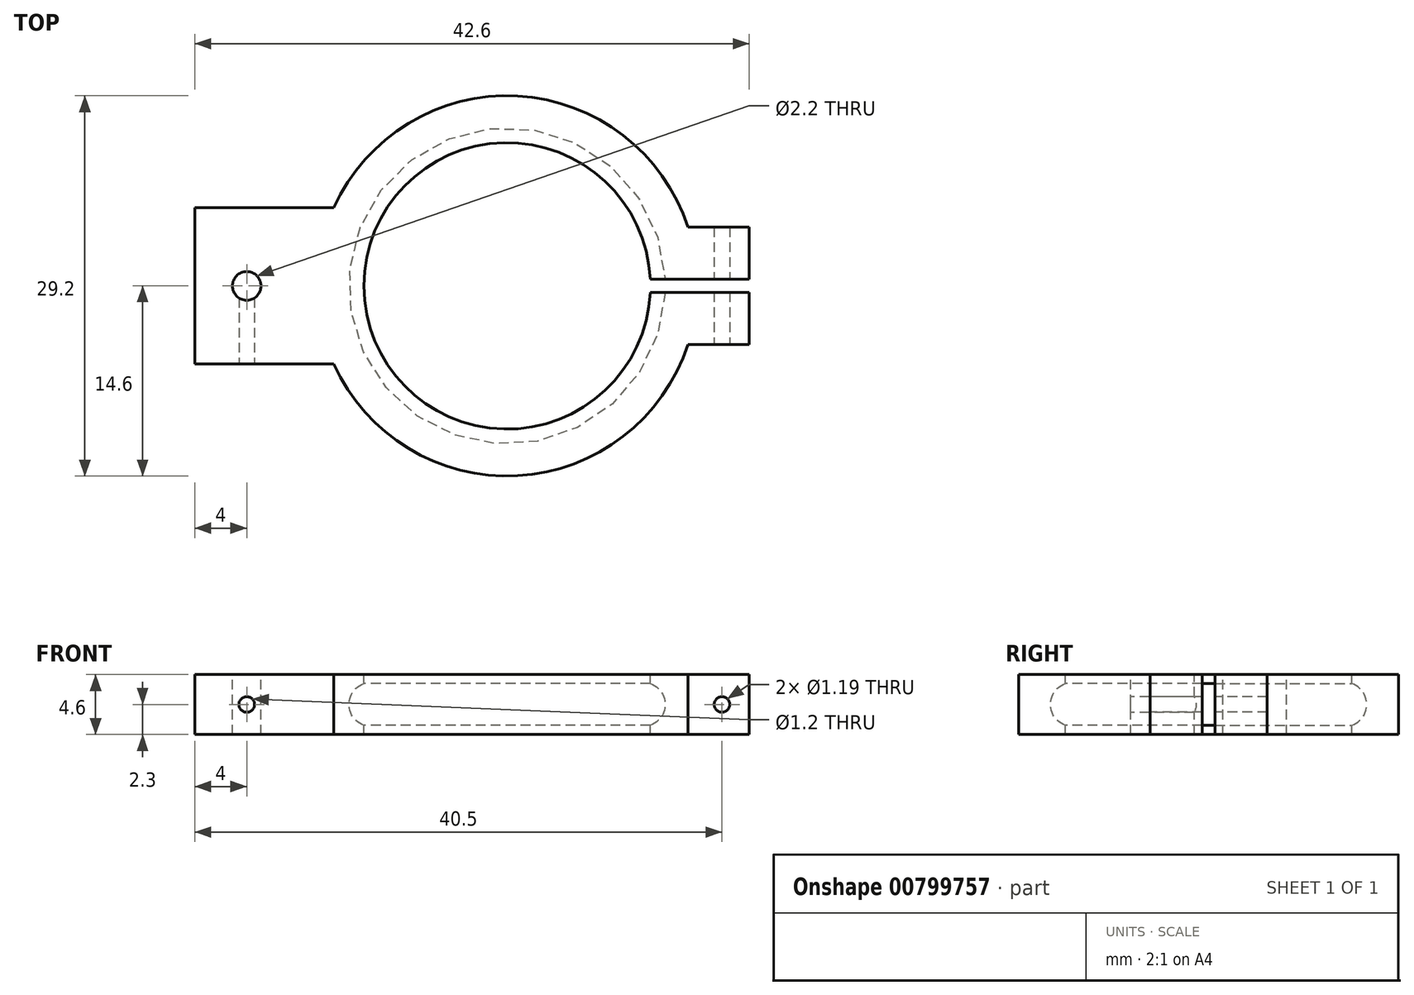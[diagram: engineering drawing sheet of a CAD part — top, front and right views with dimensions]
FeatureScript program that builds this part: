
annotation { "Feature Type Name" : "Feature", "Feature Type Description" : "" }
export const myFeature = defineFeature(function(context is Context, id is Id, definition is map)
    precondition{}
    {
        {
            var Q0;
            Q0=qCreatedBy(makeId("Front.planeOp"),FACE);
            var sketch = newSketch(context, id + "F0", { "sketchPlane" : qUnion([Q0])});
            skCircle(sketch, "E0", {"center": v(-17.36, 10.12) * mm, "radius": 2.3 * mm});
            skLineSegment(sketch, "E1", {"start": v(-6.36, 16.76) * mm, "end": v(-6.36, -1.05) * mm});
            skLineSegment(sketch, "E2", {"start": v(-17.36, 12.42) * mm, "end": v(-17.36, 7.82) * mm});
            skLineSegment(sketch, "E3", {"start": v(-17.36, 11.72) * mm, "end": v(-19.01, 11.72) * mm});
            skLineSegment(sketch, "E4", {"start": v(-17.36, 8.52) * mm, "end": v(-19.01, 8.52) * mm});
            skLineSegment(sketch, "E5", {"start": v(-18.5, 10.78) * mm, "end": v(-18.5, 9.2) * mm});
            skArc(sketch, "E6", {"start": v(-17.36, 11.72) * mm, "mid": v(-18.5, 10.12) * mm, "end": v(-17.36, 8.52) * mm});
            skLineSegment(sketch, "E7", {"start": v(-17.36, 12.42) * mm, "end": v(-20.96, 12.42) * mm});
            skLineSegment(sketch, "E8", {"start": v(-20.96, 12.42) * mm, "end": v(-20.96, 7.82) * mm});
            skLineSegment(sketch, "E9", {"start": v(-20.96, 7.82) * mm, "end": v(-17.36, 7.82) * mm});
            skSolve(sketch);
        }
        {
            var Q0;
            {var subQ3=sQuery(id+"F0.wireOp",EDGE,"E3");Q0=makeQuery(id+"F0.imprint","IMPRINT",FACE,{"disambiguationData":[TD([[makeQuery(id+"F0.imprint","IMPRINT",EDGE,{"derivedFrom":subQ3}),-1.0]])]});}
            var Q1;
            {var subQ0=sQuery(id+"F0.wireOp",EDGE,"E3");Q1=makeQuery(id+"F0.imprint","IMPRINT",FACE,{"disambiguationData":[TD([[makeQuery(id+"F0.imprint","IMPRINT",EDGE,{"derivedFrom":subQ0}),1.0]])]});}
            var Q2;
            {var subQ3=sQuery(id+"F0.wireOp",EDGE,"E4");Q2=makeQuery(id+"F0.imprint","IMPRINT",FACE,{"disambiguationData":[TD([[makeQuery(id+"F0.imprint","IMPRINT",EDGE,{"derivedFrom":subQ3}),1.0]])]});}
            var Q3;
            {var subQ5=sQuery(id+"F0.wireOp",EDGE,"E7");Q3=makeQuery(id+"F0.imprint","IMPRINT",FACE,{"disambiguationData":[TD([[makeQuery(id+"F0.imprint","IMPRINT",EDGE,{"derivedFrom":subQ5}),1.0]])]});}
            var Q4;
            Q4=sQuery(id+"F0.wireOp",EDGE,"E1");
            revolve(context, id + "F1", {"surfaceOperationType" : NewSurfaceOperationType.NEW, "entities" : qUnion([Q0, Q1, Q2, Q3]), "axis" : qUnion([Q4]), "revolveType" : RevolveType.FULL});
        }
        {
            var Q0;
            Q0=makeQuery(id+"F1.opRevolve","SWEPT_FACE",FACE,{"disambiguationData":[OSD([sQuery(id+"F0.wireOp",EDGE,"E7")])]});
            var sketch = newSketch(context, id + "F2", { "sketchPlane" : qUnion([Q0])});
            skLineSegment(sketch, "E10.bottom", {"start": v(-18.78, 6) * mm, "end": v(-30.36, 6) * mm});
            skLineSegment(sketch, "E10.top", {"start": v(-18.78, -6) * mm, "end": v(-30.36, -6) * mm});
            skLineSegment(sketch, "E10.left", {"start": v(-18.78, 6) * mm, "end": v(-18.78, -6) * mm});
            skLineSegment(sketch, "E10.right", {"start": v(-30.36, 6) * mm, "end": v(-30.36, -6) * mm});
            skLineSegment(sketch, "E11.bottom", {"start": v(6.47, 4.5) * mm, "end": v(12.24, 4.5) * mm});
            skLineSegment(sketch, "E11.top", {"start": v(6.47, -4.5) * mm, "end": v(12.24, -4.5) * mm});
            skLineSegment(sketch, "E11.left", {"start": v(6.47, 4.5) * mm, "end": v(6.47, -4.5) * mm});
            skLineSegment(sketch, "E11.right", {"start": v(12.24, 4.5) * mm, "end": v(12.24, -4.5) * mm});
            skLineSegment(sketch, "E12", {"start": v(6.47, 0.5) * mm, "end": v(12.24, 0.5) * mm});
            skLineSegment(sketch, "E13", {"start": v(6.47, -0.5) * mm, "end": v(12.24, -0.5) * mm});
            skPoint(sketch, "E14", {"position": v(-6.36, 0) * mm});
            skCircle(sketch, "E15", {"center": v(-26.36, 0) * mm, "radius": 1.1 * mm});
            skSolve(sketch);
        }
        {
            var Q0;
            {var subQ0=sQuery(id+"F2.wireOp",EDGE,"E10.left");Q0=makeQuery(id+"F2.imprint","IMPRINT",FACE,{"disambiguationData":[TD([[makeQuery(id+"F2.imprint","IMPRINT",EDGE,{"derivedFrom":subQ0}),-1.0]])]});}
            var Q1;
            {var subQ0=sQuery(id+"F2.wireOp",EDGE,"E11.right");var subQ1=sQuery(id+"F2.wireOp",EDGE,"E11.bottom");var subQ2=makeQuery(id+"F2.imprint","INTERSECT",VERTEX,{"derivedFrom":[subQ1,subQ0]});Q1=makeQuery(id+"F2.imprint","IMPRINT",FACE,{"disambiguationData":[TD([[makeQuery(id+"F2.imprint","IMPRINT",EDGE,{"disambiguationData":[TD([[subQ2,-1.0]])],"derivedFrom":subQ0}),-1.0]])]});}
            var Q2;
            {var subQ0=sQuery(id+"F2.wireOp",EDGE,"E11.right");var subQ1=sQuery(id+"F2.wireOp",EDGE,"E11.top");var subQ2=makeQuery(id+"F2.imprint","INTERSECT",VERTEX,{"derivedFrom":[subQ1,subQ0]});Q2=makeQuery(id+"F2.imprint","IMPRINT",FACE,{"disambiguationData":[TD([[makeQuery(id+"F2.imprint","IMPRINT",EDGE,{"disambiguationData":[TD([[subQ2,1.0]])],"derivedFrom":subQ0}),-1.0]])]});}
            var Q3;
            {var subQ0=sQuery(id+"F2.wireOp",EDGE,"E11.left");var subQ1=sQuery(id+"F2.wireOp",EDGE,"E11.bottom");var subQ2=makeQuery(id+"F2.imprint","INTERSECT",VERTEX,{"derivedFrom":[subQ1,subQ0]});Q3=makeQuery(id+"F2.imprint","IMPRINT",FACE,{"disambiguationData":[TD([[makeQuery(id+"F2.imprint","IMPRINT",EDGE,{"disambiguationData":[TD([[subQ2,-1.0]])],"derivedFrom":subQ0}),1.0]])]});}
            var Q4;
            {var subQ0=sQuery(id+"F2.wireOp",EDGE,"E11.left");var subQ1=sQuery(id+"F2.wireOp",EDGE,"E11.top");var subQ2=makeQuery(id+"F2.imprint","INTERSECT",VERTEX,{"derivedFrom":[subQ1,subQ0]});Q4=makeQuery(id+"F2.imprint","IMPRINT",FACE,{"disambiguationData":[TD([[makeQuery(id+"F2.imprint","IMPRINT",EDGE,{"disambiguationData":[TD([[subQ2,1.0]])],"derivedFrom":subQ0}),1.0]])]});}
            var Q5;
            {var subQ0=sQuery(id+"F2.wireOp",EDGE,"E12");var subQ1=sQuery(id+"F2.wireOp",EDGE,"E11.right");var subQ2=makeQuery(id+"F2.imprint","INTERSECT",VERTEX,{"derivedFrom":[subQ1,subQ0]});Q5=makeQuery(id+"F2.imprint","IMPRINT",FACE,{"disambiguationData":[TD([[makeQuery(id+"F2.imprint","IMPRINT",EDGE,{"disambiguationData":[TD([[subQ2,-1.0]])],"derivedFrom":subQ1}),-1.0]])]});}
            var Q6;
            {var subQ0=sQuery(id+"F2.wireOp",EDGE,"E12");var subQ1=sQuery(id+"F2.wireOp",EDGE,"E11.left");var subQ2=makeQuery(id+"F2.imprint","INTERSECT",VERTEX,{"derivedFrom":[subQ1,subQ0]});Q6=makeQuery(id+"F2.imprint","IMPRINT",FACE,{"disambiguationData":[TD([[makeQuery(id+"F2.imprint","IMPRINT",EDGE,{"disambiguationData":[TD([[subQ2,-1.0]])],"derivedFrom":subQ1}),1.0]])]});}
            var Q7;
            {var subQ0=sQuery(id+"F2.wireOp",EDGE,"E10.right");Q7=makeQuery(id+"F2.imprint","IMPRINT",FACE,{"disambiguationData":[TD([[makeQuery(id+"F2.imprint","IMPRINT",EDGE,{"derivedFrom":subQ0}),1.0]])]});}
            extrude(context, id + "F3", {"entities" : qUnion([Q0, Q1, Q2, Q3, Q4, Q5, Q6, Q7]), "operationType" : NewBodyOperationType.ADD, "oppositeDirection" : true, "depth" : 4.6 * mm, "offsetDistance" : 25 * mm});
        }
        {
            var Q0;
            Q0=makeQuery(id+"F3.opExtrude","SWEPT_FACE",FACE,{"disambiguationData":[OSD([sQuery(id+"F2.wireOp",EDGE,"E10.top")])]});
            var sketch = newSketch(context, id + "F4", { "sketchPlane" : qUnion([Q0])});
            skCircle(sketch, "E16", {"center": v(-26.36, 10.12) * mm, "radius": 0.6 * mm});
            skPoint(sketch, "E16.centerSnap0", {"position": v(-30.36, 10.12) * mm});
            skSolve(sketch);
        }
        {
            var Q0;
            Q0=makeQuery(id+"F4.imprint","IMPRINT",FACE,{"disambiguationData":[TD([[makeQuery(id+"F4.imprint","IMPRINT",EDGE,{"derivedFrom":sQuery(id+"F4.wireOp",EDGE,"E16")}),1.0]])]});
            extrude(context, id + "F5", {"entities" : qUnion([Q0]), "operationType" : NewBodyOperationType.REMOVE, "oppositeDirection" : true, "depth" : 6 * mm, "offsetDistance" : 25 * mm});
        }
        {
            var Q0;
            Q0=makeQuery(id+"F3.opExtrude","SWEPT_FACE",FACE,{"disambiguationData":[OSD([sQuery(id+"F2.wireOp",EDGE,"E11.top")])]});
            var sketch = newSketch(context, id + "F6", { "sketchPlane" : qUnion([Q0])});
            skCircle(sketch, "E17", {"center": v(10.14, 10.12) * mm, "radius": 0.6 * mm});
            skPoint(sketch, "E17.centerSnap0", {"position": v(12.24, 10.12) * mm});
            skSolve(sketch);
        }
        {
            var Q0;
            Q0=makeQuery(id+"F6.imprint","IMPRINT",FACE,{"disambiguationData":[TD([[makeQuery(id+"F6.imprint","IMPRINT",EDGE,{"derivedFrom":sQuery(id+"F6.wireOp",EDGE,"E17")}),1.0]])]});
            extrude(context, id + "F7", {"entities" : qUnion([Q0]), "operationType" : NewBodyOperationType.REMOVE, "oppositeDirection" : true, "depth" : 25 * mm, "offsetDistance" : 25 * mm});
        }
        {
            var Q0;
            Q0=makeQuery(id+"F3.boolean.opBoolean","MERGE",FACE,{"derivedFrom":[makeQuery(id+"F1.opRevolve","SWEPT_FACE",FACE,{"disambiguationData":[OSD([sQuery(id+"F0.wireOp",EDGE,"E7")])]}),makeQuery(id+"F3.opExtrude","CAP_FACE",FACE,{"disambiguationData":[OSD([sQuery(id+"F2.wireOp",EDGE,"E10.bottom"),sQuery(id+"F2.wireOp",EDGE,"E10.top"),sQuery(id+"F2.wireOp",EDGE,"E10.left"),sQuery(id+"F2.wireOp",EDGE,"E10.right"),sQuery(id+"F2.wireOp",EDGE,"E15")])],"isStart":true}),makeQuery(id+"F3.opExtrude","CAP_FACE",FACE,{"disambiguationData":[OSD([sQuery(id+"F2.wireOp",EDGE,"E11.bottom"),sQuery(id+"F2.wireOp",EDGE,"E11.top"),sQuery(id+"F2.wireOp",EDGE,"E11.left"),sQuery(id+"F2.wireOp",EDGE,"E11.right")])],"isStart":true})]});
            var sketch = newSketch(context, id + "F8", { "sketchPlane" : qUnion([Q0])});
            skLineSegment(sketch, "E18.bottom", {"start": v(3.3, 0.5) * mm, "end": v(13.94, 0.5) * mm});
            skLineSegment(sketch, "E18.top", {"start": v(3.3, -0.5) * mm, "end": v(13.94, -0.5) * mm});
            skLineSegment(sketch, "E18.left", {"start": v(3.3, 0.5) * mm, "end": v(3.3, -0.5) * mm});
            skLineSegment(sketch, "E18.right", {"start": v(13.94, 0.5) * mm, "end": v(13.94, -0.5) * mm});
            skSolve(sketch);
        }
        {
            var Q0;
            {var subQ0=sQuery(id+"F8.wireOp",EDGE,"E18.bottom");var subQ1=makeQuery(id+"F3.opExtrude","CAP_EDGE",EDGE,{"disambiguationData":[OSD([sQuery(id+"F2.wireOp",EDGE,"E11.right")])],"isStart":true});var subQ2=makeQuery(id+"F8.imprint","INTERSECT",VERTEX,{"derivedFrom":[subQ1,subQ0]});Q0=makeQuery(id+"F8.imprint","IMPRINT",FACE,{"disambiguationData":[TD([[makeQuery(id+"F8.imprint","IMPRINT",EDGE,{"disambiguationData":[TD([[subQ2,-1.0]])],"derivedFrom":subQ1}),-1.0]])]});}
            var Q1;
            {var subQ0=sQuery(id+"F8.wireOp",EDGE,"E18.left");Q1=makeQuery(id+"F8.imprint","IMPRINT",FACE,{"disambiguationData":[TD([[makeQuery(id+"F8.imprint","IMPRINT",EDGE,{"derivedFrom":subQ0}),1.0]])]});}
            var Q2;
            {var subQ0=sQuery(id+"F8.wireOp",EDGE,"E18.right");Q2=makeQuery(id+"F8.imprint","IMPRINT",FACE,{"disambiguationData":[TD([[makeQuery(id+"F8.imprint","IMPRINT",EDGE,{"derivedFrom":subQ0}),-1.0]])]});}
            extrude(context, id + "F9", {"entities" : qUnion([Q0, Q1, Q2]), "operationType" : NewBodyOperationType.REMOVE, "oppositeDirection" : true, "depth" : 25 * mm, "offsetDistance" : 25 * mm});
        }
    });
